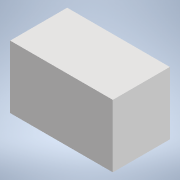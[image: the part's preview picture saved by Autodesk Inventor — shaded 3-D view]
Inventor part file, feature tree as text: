
AUTODESK INVENTOR PART (.ipt)
format: ipt  version: 2020 (Build 240168000, 168)  size: 84,480 bytes
history: native  units: mm
features: extrude x1, sketch x1
ambient origin geometry x8: Origin, YZ Plane, XZ Plane, XY Plane, X Axis, Y Axis, Z Axis, Center Point
bodies: Solid1 (feature_tree)
feature tree (2):
  extrude  "Extrusion1"  Depth=180.0mm
  sketch  "Sketch1"  dims[d0=110.0mm d1=180.0mm d2=100.0mm d3=0.0mm]
